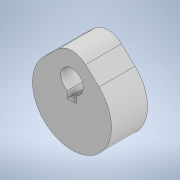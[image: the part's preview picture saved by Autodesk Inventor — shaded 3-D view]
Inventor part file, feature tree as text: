
AUTODESK INVENTOR PART (.ipt)
format: ipt  version: 2021 (Build 250183000, 183)  size: 112,640 bytes
history: native  units: mm
features: extrude x1, sketch x1
ambient origin geometry x8: Origin, YZ Plane, XZ Plane, XY Plane, X Axis, Y Axis, Z Axis, Center Point
bodies: Solid1 (feature_tree)
feature tree (2):
  extrude  "Extrusion1"  Depth=6.0mm
  sketch  "Sketch1"  dims[d0=17.5mm d1=6.0mm d2=8.75mm d3=5.0mm d4=4.5mm d5=8.0mm d6=0.0mm d7=2.0mm d8=1.5mm]
